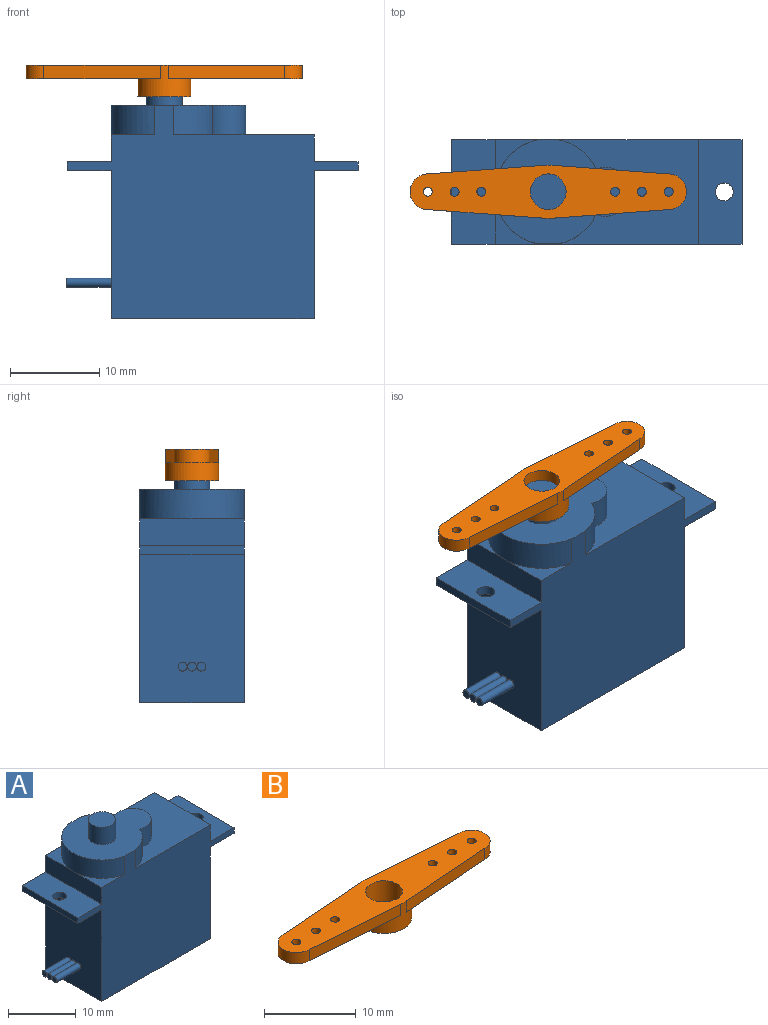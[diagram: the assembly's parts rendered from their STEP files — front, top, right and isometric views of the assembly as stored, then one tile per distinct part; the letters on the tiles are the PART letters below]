
ASSEMBLY  parts=2 mates=1
PART A: 31 faces, bbox 32.7x11.7x27.1 mm
  f0: plane 15.71x11.7mm, normal (0,0,1), area 125.7mm2, adj f3,f4,f6,f19,f20,f21
  f1: plane 5.85x4.86mm, normal (0,0,1), area 7.1mm2, adj f2,f4,f18
  f2: plane 11.7x3mm, normal (-1,0,0), area 35.1mm2, adj f1,f4,f6,f9,f17
  f3: plane 11.7x3mm, normal (1,0,0), area 35.1mm2, adj f0,f4,f6,f13
  f4: plane 32.6x23.9mm, normal (0,1,0), area 485.7mm2, adj f0,f1,f2,f3,f5,f7,f8,f10
  f5: plane 16.6x11.7mm, normal (-1,0,0), area 191.9mm2, adj f4,f6,f8,f16,f25,f27,f29
  f6: plane 32.6x23.9mm, normal (0,-1,0), area 485.7mm2, adj f0,f2,f3,f5,f7,f8,f9,f10
  f7: plane 16.6x11.7mm, normal (1,0,0), area 194.2mm2, adj f4,f6,f8,f12
  f8: plane 22.75x11.7mm, normal (0,0,-1), area 266.2mm2, adj f4,f5,f6,f7
  f9: plane 5.85x4.86mm, normal (0,0,1), area 7.1mm2, adj f2,f6,f18
  f10: plane 11.7x1mm, normal (1,0,0), area 11.7mm2, adj f4,f6,f12,f13
  f11: cylinder r=1mm len=2mm, axis (0,0,1), area 6.3mm2, adj f12,f13
  f12: plane 11.7x4.93mm, normal (0,0,-1), area 54.5mm2, adj f4,f6,f7,f10,f11
  f13: plane 11.7x4.93mm, normal (0,0,1), area 54.5mm2, adj f3,f4,f6,f10,f11
  f14: cylinder r=1mm len=2mm, axis (0,0,1), area 6.3mm2, adj f16,f17
  f15: plane 11.7x1mm, normal (-1,0,0), area 11.7mm2, adj f4,f6,f16,f17
  f16: plane 11.7x4.93mm, normal (0,0,-1), area 54.5mm2, adj f4,f5,f6,f14,f15
  f17: plane 11.7x4.93mm, normal (0,0,1), area 54.5mm2, adj f2,f4,f6,f14,f15
  f18: cylinder r=5.95mm len=11.7mm, axis (0,0,-1), area 54.5mm2, adj f1,f4,f6,f9,f22
  f19: cylinder r=5.95mm len=4.29mm, axis (0,0,-1), area 18.5mm2, adj f0,f6,f20,f22
  f20: cylinder r=2.75mm len=5.5mm, axis (0,0,-1), area 35.4mm2, adj f0,f19,f21,f22
  f21: cylinder r=5.95mm len=4.29mm, axis (0,0,-1), area 18.5mm2, adj f0,f4,f20,f22
  f22: plane 15.1x11.7mm, normal (0,0,1), area 113.8mm2, adj f4,f6,f18,f19,f20,f21,f23
  f23: cylinder r=2mm len=4mm, axis (0,0,-1), area 39.6mm2, adj f22,f24
  f24: plane 4x4mm, normal (0,0,1), area 12.6mm2, adj f23
  f25: cylinder r=0.5mm len=5mm, axis (1,0,0), area 15.7mm2, adj f5,f26
  f26: plane 1x1mm, normal (-1,0,0), area 0.8mm2, adj f25
  f27: cylinder r=0.5mm len=5mm, axis (1,0,0), area 15.7mm2, adj f5,f28
  f28: plane 1x1mm, normal (-1,0,0), area 0.8mm2, adj f27
  f29: cylinder r=0.5mm len=5mm, axis (1,0,0), area 15.7mm2, adj f5,f30
  f30: plane 1x1mm, normal (-1,0,0), area 0.8mm2, adj f29
PART B: 18 faces, bbox 31x6x3.5 mm
  f0: cylinder r=2mm len=4mm, axis (0,0,1), area 44mm2, adj f2,f17
  f1: cylinder r=3mm len=6mm, axis (0,0,1), area 40.4mm2, adj f2,f3,f4,f5,f7,f8,f16,f17
  f2: plane 6x6mm, normal (0,0,-1), area 15.7mm2, adj f0,f1
  f3: plane 15.06x5.93mm, normal (0,0,-1), area 57.3mm2, adj f1,f5,f6,f7,f13,f14,f15
  f4: plane 15.06x5.93mm, normal (0,0,-1), area 57.3mm2, adj f1,f8,f9,f10,f11,f12,f16
  f5: plane 13.06x1.5mm, normal (-0.07,1,0), area 19.6mm2, adj f1,f3,f6,f17
  f6: cylinder r=2mm len=4mm, axis (0,0,-1), area 9.4mm2, adj f3,f5,f7,f17
  f7: plane 13.06x1.5mm, normal (-0.07,-1,0), area 19.6mm2, adj f1,f3,f6,f17
  f8: plane 13.06x1.5mm, normal (0.07,-1,0), area 19.6mm2, adj f1,f4,f9,f17
  f9: cylinder r=2mm len=4mm, axis (0,0,-1), area 9.4mm2, adj f4,f8,f16,f17
  f10: cylinder r=0.5mm len=1.5mm, axis (0,0,-1), area 4.7mm2, adj f4,f17
  f11: cylinder r=0.5mm len=1.5mm, axis (0,0,-1), area 4.7mm2, adj f4,f17
  f12: cylinder r=0.5mm len=1.5mm, axis (0,0,-1), area 4.7mm2, adj f4,f17
  f13: cylinder r=0.5mm len=1.5mm, axis (0,0,-1), area 4.7mm2, adj f3,f17
  f14: cylinder r=0.5mm len=1.5mm, axis (0,0,-1), area 4.7mm2, adj f3,f17
  f15: cylinder r=0.5mm len=1.5mm, axis (0,0,-1), area 4.7mm2, adj f3,f17
  f16: plane 13.06x1.5mm, normal (0.07,1,0), area 19.6mm2, adj f1,f4,f9,f17
  f17: plane 31x6mm, normal (0,0,1), area 130.3mm2, adj f0,f1,f5,f6,f7,f8,f9,f10
PLACE A at identity fixed
PLACE B t=(0,0,-0.15)mm
MATE fastened A.f18 <-> B.f0  axis (0,0,1) through (-5.42,0,6.3)mm
